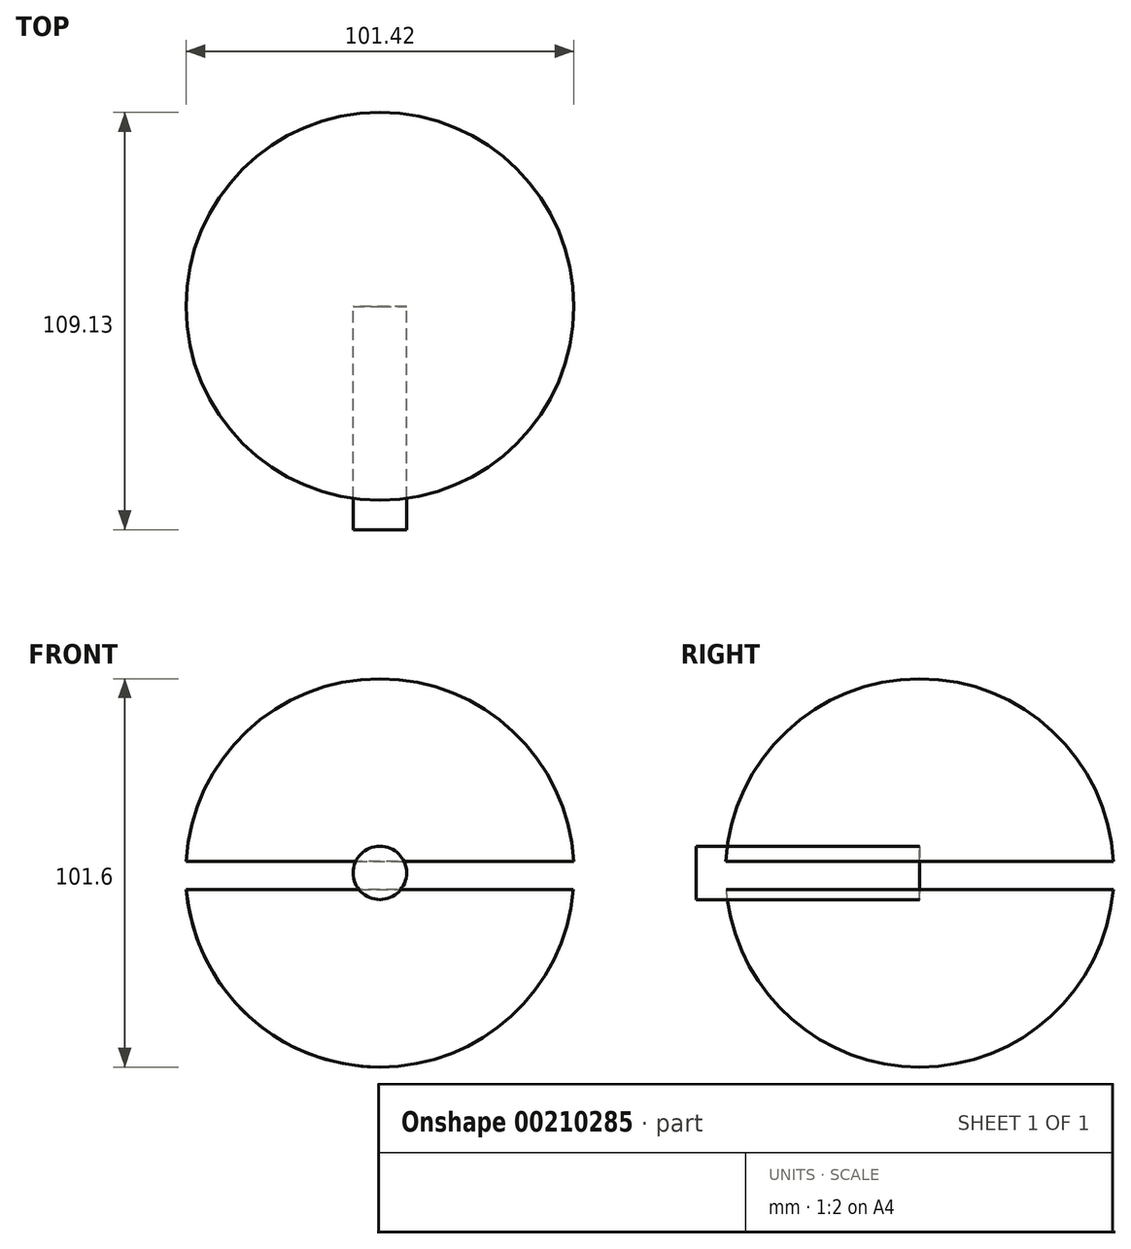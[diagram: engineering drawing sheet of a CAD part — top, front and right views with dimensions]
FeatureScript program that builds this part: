
annotation { "Feature Type Name" : "Feature", "Feature Type Description" : "" }
export const myFeature = defineFeature(function(context is Context, id is Id, definition is map)
    precondition{}
    {
        {
            var Q0;
            Q0=qCreatedBy(makeId("Front.planeOp"),FACE);
            var sketch = newSketch(context, id + "F0", { "sketchPlane" : qUnion([Q0])});
            skCircle(sketch, "E0", {"center": v(0, 0) * mm, "radius": 50.8 * mm});
            skLineSegment(sketch, "E1", {"start": v(0, 56.62) * mm, "end": v(0, -60.9) * mm});
            skLineSegment(sketch, "E2", {"start": v(-62.47, 3) * mm, "end": v(69.31, 3) * mm});
            skLineSegment(sketch, "E3", {"start": v(-61.61, -4.42) * mm, "end": v(71.31, -4.42) * mm});
            skSolve(sketch);
        }
        {
            var Q0;
            {var subQ0=sQuery(id+"F0.wireOp",EDGE,"E1");var subQ1=sQuery(id+"F0.wireOp",EDGE,"E0");var subQ2=makeQuery(id+"F0.imprint","INTERSECT",VERTEX,{"disambiguationData":[OD(0.0)],"derivedFrom":[subQ1,subQ0]});Q0=makeQuery(id+"F0.imprint","IMPRINT",FACE,{"disambiguationData":[TD([[makeQuery(id+"F0.imprint","IMPRINT",EDGE,{"disambiguationData":[TD([[subQ2,1.0]])],"derivedFrom":subQ1}),1.0]])]});}
            var Q1;
            {var subQ0=sQuery(id+"F0.wireOp",EDGE,"E1");var subQ1=sQuery(id+"F0.wireOp",EDGE,"E0");var subQ2=makeQuery(id+"F0.imprint","INTERSECT",VERTEX,{"disambiguationData":[OD(1.0)],"derivedFrom":[subQ1,subQ0]});Q1=makeQuery(id+"F0.imprint","IMPRINT",FACE,{"disambiguationData":[TD([[makeQuery(id+"F0.imprint","IMPRINT",EDGE,{"disambiguationData":[TD([[subQ2,-1.0]])],"derivedFrom":subQ1}),1.0]])]});}
            var Q2;
            Q2=sQuery(id+"F0.wireOp",EDGE,"E1");
            revolve(context, id + "F1", {"entities" : qUnion([Q0, Q1]), "axis" : qUnion([Q2]), "revolveType" : RevolveType.FULL});
        }
        {
            var Q0;
            Q0=qCreatedBy(makeId("Front.planeOp"),FACE);
            var sketch = newSketch(context, id + "F2", { "sketchPlane" : qUnion([Q0])});
            skCircle(sketch, "E4", {"center": v(0, 0) * mm, "radius": 50.6 * mm});
            skLineSegment(sketch, "E5", {"start": v(0, 56.34) * mm, "end": v(0, -61.47) * mm});
            skLineSegment(sketch, "E6.bottom", {"start": v(-42.93, -4.14) * mm, "end": v(46.64, -4.14) * mm});
            skLineSegment(sketch, "E6.top", {"start": v(-42.93, 3) * mm, "end": v(46.64, 3) * mm});
            skLineSegment(sketch, "E6.left", {"start": v(-42.93, -4.14) * mm, "end": v(-42.93, 3) * mm});
            skLineSegment(sketch, "E6.right", {"start": v(46.64, -4.14) * mm, "end": v(46.64, 3) * mm});
            skSolve(sketch);
        }
        {
            var Q0;
            {var subQ0=sQuery(id+"F0.wireOp",EDGE,"E2");var subQ1=sQuery(id+"F0.wireOp",EDGE,"E0");var subQ2=makeQuery(id+"F0.imprint","INTERSECT",VERTEX,{"disambiguationData":[OD(1.0)],"derivedFrom":[subQ1,subQ0]});Q0=makeQuery(id+"F0.imprint","IMPRINT",FACE,{"disambiguationData":[TD([[makeQuery(id+"F0.imprint","IMPRINT",EDGE,{"disambiguationData":[TD([[subQ2,-1.0]])],"derivedFrom":subQ1}),1.0]])]});}
            var Q1;
            Q1=sQuery(id+"F2.wireOp",EDGE,"E5");
            revolve(context, id + "F3", {"entities" : qUnion([Q0]), "axis" : qUnion([Q1]), "revolveType" : RevolveType.FULL});
        }
        {
            var Q0;
            Q0=qCreatedBy(makeId("Front.planeOp"),FACE);
            var sketch = newSketch(context, id + "F4", { "sketchPlane" : qUnion([Q0])});
            skCircle(sketch, "E7", {"center": v(0, 0) * mm, "radius": 10.25 * mm});
            skSolve(sketch);
        }
        {
            var Q0;
            Q0=qCreatedBy(makeId("Front.planeOp"),FACE);
            var sketch = newSketch(context, id + "F5", { "sketchPlane" : qUnion([Q0])});
            skCircle(sketch, "E8", {"center": v(0, 0) * mm, "radius": 6.99 * mm});
            skSolve(sketch);
        }
        {
            var Q0;
            Q0 = qSketchRegion(id + "F5", true);
            var Q1;
            Q1=makeQuery(id+"F5YkR20gDRIrWvJ_3.opExtrude","CAP_FACE",FACE,{"disambiguationData":[OSD([sQuery(id+"F4.wireOp",EDGE,"E7")])],"isStart":false});
            extrude(context, id + "F6", {"entities" : qUnion([Q0, Q1]), "depth" : 58.42 * mm});
        }
    });
